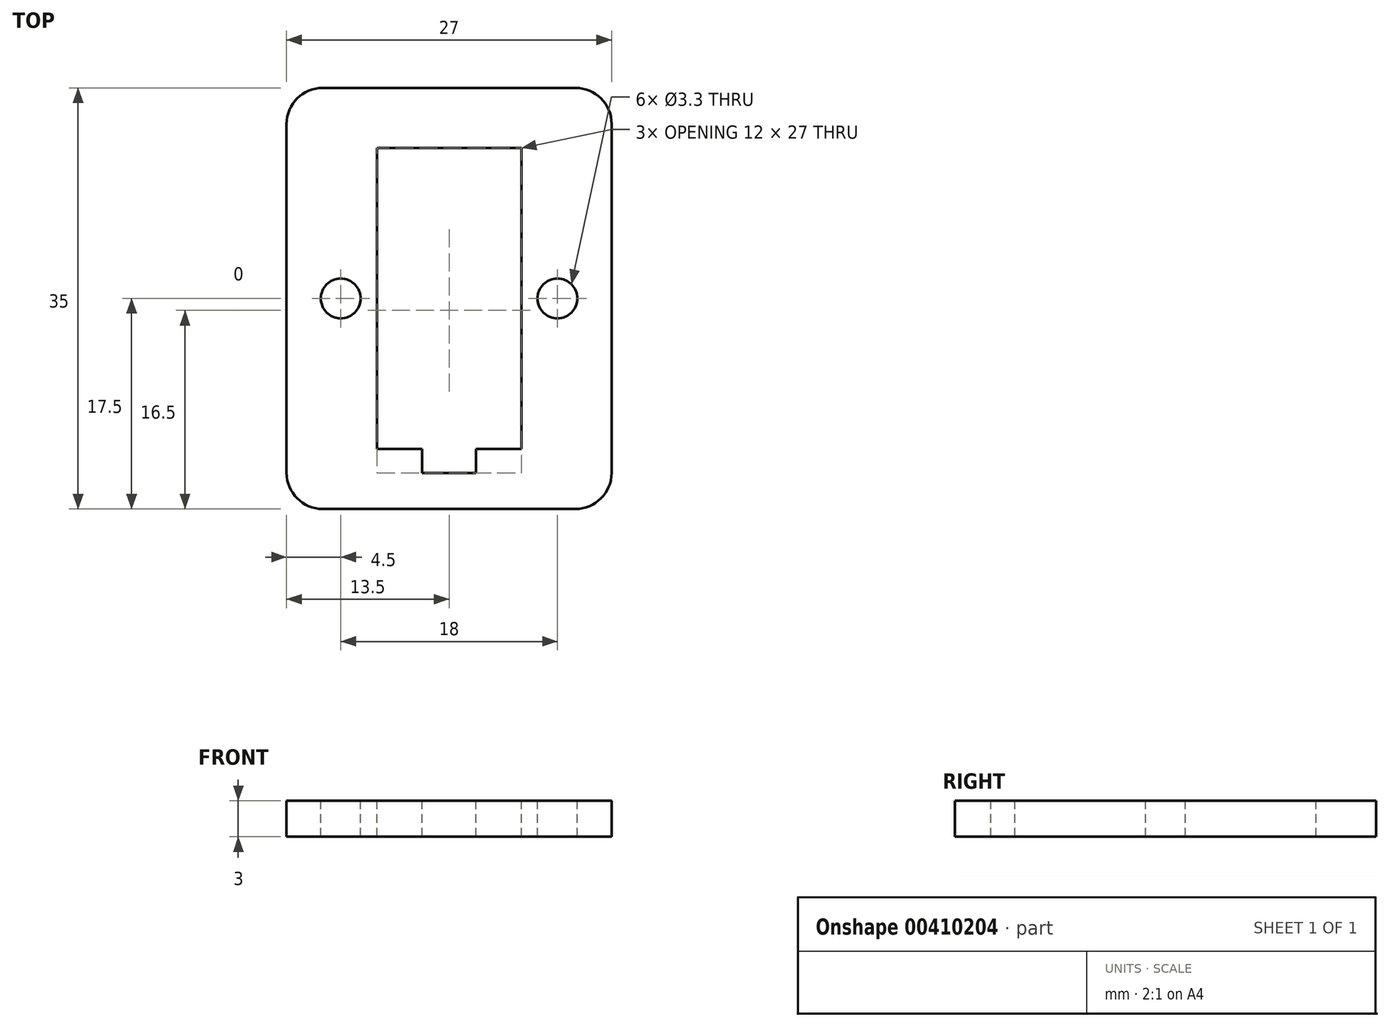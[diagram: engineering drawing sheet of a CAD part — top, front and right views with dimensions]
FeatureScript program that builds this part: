
annotation { "Feature Type Name" : "Feature", "Feature Type Description" : "" }
export const myFeature = defineFeature(function(context is Context, id is Id, definition is map)
    precondition{}
    {
        {
            var Q0;
            Q0=qCreatedBy(makeId("Top.planeOp"),FACE);
            var sketch = newSketch(context, id + "F0", { "sketchPlane" : qUnion([Q0])});
            skLineSegment(sketch, "E0.bottom", {"start": v(-10.5, 17.5) * mm, "end": v(10.5, 17.5) * mm});
            skLineSegment(sketch, "E0.top", {"start": v(-10.5, -17.5) * mm, "end": v(10.5, -17.5) * mm});
            skLineSegment(sketch, "E0.left", {"start": v(-13.5, 14.5) * mm, "end": v(-13.5, -14.5) * mm});
            skLineSegment(sketch, "E0.right", {"start": v(13.5, 14.5) * mm, "end": v(13.5, -14.5) * mm});
            skPoint(sketch, "E0.middle", {"position": v(0, 0) * mm});
            skPoint(sketch, "E1.visualSharp", {"position": v(-13.5, 17.5) * mm});
            skArc(sketch, "E1.filletArc", {"start": v(-10.5, 17.5) * mm, "mid": v(-12.62, 16.62) * mm, "end": v(-13.5, 14.5) * mm});
            skPoint(sketch, "E2.visualSharp", {"position": v(13.5, 17.5) * mm});
            skArc(sketch, "E2.filletArc", {"start": v(13.5, 14.5) * mm, "mid": v(12.62, 16.62) * mm, "end": v(10.5, 17.5) * mm});
            skPoint(sketch, "E3.visualSharp", {"position": v(13.5, -17.5) * mm});
            skArc(sketch, "E3.filletArc", {"start": v(10.5, -17.5) * mm, "mid": v(12.62, -16.62) * mm, "end": v(13.5, -14.5) * mm});
            skPoint(sketch, "E4.visualSharp", {"position": v(-13.5, -17.5) * mm});
            skArc(sketch, "E4.filletArc", {"start": v(-13.5, -14.5) * mm, "mid": v(-12.62, -16.62) * mm, "end": v(-10.5, -17.5) * mm});
            skSolve(sketch);
        }
        {
            var Q0;
            Q0=qSketchRegion(id+"F0",true);
            extrude(context, id + "F1", {"entities" : qUnion([Q0]), "depth" : 3 * mm});
        }
        {
            var Q0;
            Q0=makeQuery(id+"F1.opExtrude","CAP_FACE",FACE,{"disambiguationData":[OSD([sQuery(id+"F0.wireOp",EDGE,"E0.bottom"),sQuery(id+"F0.wireOp",EDGE,"E0.top"),sQuery(id+"F0.wireOp",EDGE,"E0.left"),sQuery(id+"F0.wireOp",EDGE,"E0.right"),sQuery(id+"F0.wireOp",EDGE,"E1.filletArc"),sQuery(id+"F0.wireOp",EDGE,"E2.filletArc"),sQuery(id+"F0.wireOp",EDGE,"E3.filletArc"),sQuery(id+"F0.wireOp",EDGE,"E4.filletArc")])],"isStart":false});
            var sketch = newSketch(context, id + "F2", { "sketchPlane" : qUnion([Q0])});
            skCircle(sketch, "E5", {"center": v(-9, 0) * mm, "radius": 1.65 * mm});
            skCircle(sketch, "E6", {"center": v(9, 0) * mm, "radius": 1.65 * mm});
            skSolve(sketch);
        }
        {
            var Q0;
            Q0=sQuery(id+"F2.wireOp",VERTEX,"E5.center");
            var Q1;
            Q1=sQuery(id+"F2.wireOp",VERTEX,"E6.center");
            var Q2;
            Q2=makeQuery(id+"F1.opExtrude","SWEPT_BODY",BODY,{"disambiguationData":[OSD([sQuery(id+"F0.wireOp",EDGE,"E0.bottom"),sQuery(id+"F0.wireOp",EDGE,"E0.top"),sQuery(id+"F0.wireOp",EDGE,"E0.left"),sQuery(id+"F0.wireOp",EDGE,"E0.right"),sQuery(id+"F0.wireOp",EDGE,"E1.filletArc"),sQuery(id+"F0.wireOp",EDGE,"E2.filletArc"),sQuery(id+"F0.wireOp",EDGE,"E3.filletArc"),sQuery(id+"F0.wireOp",EDGE,"E4.filletArc")])]});
            hole(context, id + "F3", {"style" : HoleStyle.SIMPLE, "endStyle" : HoleEndStyle.THROUGH, "holeDiameter" : 3.3 * mm, "locations" : qUnion([Q0, Q1]), "scope" : qUnion([Q2]), "isTappedThrough" : true});
        }
        {
            var Q0;
            Q0=makeQuery(id+"F1.opExtrude","CAP_FACE",FACE,{"disambiguationData":[OSD([sQuery(id+"F0.wireOp",EDGE,"E0.bottom"),sQuery(id+"F0.wireOp",EDGE,"E0.top"),sQuery(id+"F0.wireOp",EDGE,"E0.left"),sQuery(id+"F0.wireOp",EDGE,"E0.right"),sQuery(id+"F0.wireOp",EDGE,"E1.filletArc"),sQuery(id+"F0.wireOp",EDGE,"E2.filletArc"),sQuery(id+"F0.wireOp",EDGE,"E3.filletArc"),sQuery(id+"F0.wireOp",EDGE,"E4.filletArc")])],"isStart":false});
            var sketch = newSketch(context, id + "F4", { "sketchPlane" : qUnion([Q0])});
            skLineSegment(sketch, "E7.bottom", {"start": v(-6, 12.5) * mm, "end": v(6, 12.5) * mm});
            skLineSegment(sketch, "E7.top", {"start": v(-6, -12.5) * mm, "end": v(-2.25, -12.5) * mm});
            skLineSegment(sketch, "E7.left", {"start": v(-6, 12.5) * mm, "end": v(-6, -12.5) * mm});
            skLineSegment(sketch, "E7.right", {"start": v(6, 12.5) * mm, "end": v(6, -12.5) * mm});
            skPoint(sketch, "E7.middle", {"position": v(0, 0) * mm});
            skLineSegment(sketch, "E8.bottom", {"start": v(-2.25, -14.5) * mm, "end": v(2.25, -14.5) * mm});
            skLineSegment(sketch, "E8.left", {"start": v(-2.25, -14.5) * mm, "end": v(-2.25, -12.5) * mm});
            skLineSegment(sketch, "E8.right", {"start": v(2.25, -14.5) * mm, "end": v(2.25, -12.5) * mm});
            skLineSegment(sketch, "E9.trimOffspring", {"start": v(2.25, -12.5) * mm, "end": v(6, -12.5) * mm});
            skSolve(sketch);
        }
        {
            var Q0;
            Q0=qSketchRegion(id+"F4",true);
            extrude(context, id + "F5", {"entities" : qUnion([Q0]), "operationType" : NewBodyOperationType.REMOVE, "oppositeDirection" : true, "depth" : 25 * mm});
        }
    });
